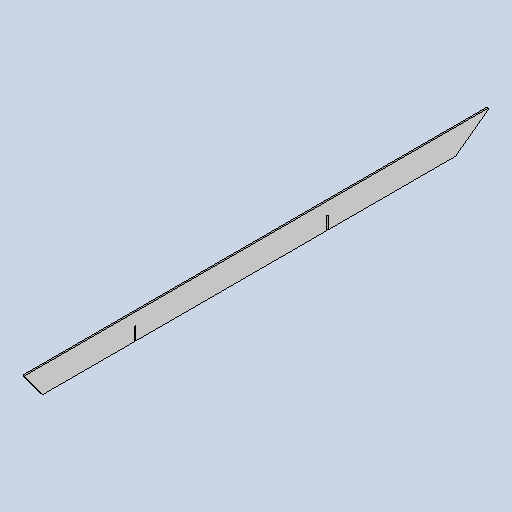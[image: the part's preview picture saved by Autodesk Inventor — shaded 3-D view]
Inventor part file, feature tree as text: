
AUTODESK INVENTOR PART (.ipt)
format: ipt  version: 2025 (Build 290162010, 162A)  size: 151,040 bytes
history: native  units: mm
features: other x3, sketch x2, sheet_metal_op x1, chamfer x1, extrude x1
ambient origin geometry x8: Origin, YZ Plane, XZ Plane, XY Plane, X Axis, Y Axis, Z Axis, Center Point
bodies: Body1 (feature_tree)
feature tree (8):
  sheet_metal_op  "Face1"
  other  "Corner Chamfer1"
  chamfer  "Corner Round1"
  extrude  "Extrusion1"  Depth=920.0mm
  sketch  "Sketch2"  dims[d3=380.0mm d6=380.0mm d7=380.0mm d28=920.0mm]
  other  "Plate2"
  sketch  "Sketch3"  dims[d29=50.0mm d30=3.0mm d31=6.335545mm d32=9.372418mm d33=3.0mm d34=6.0mm d35=45.0deg d36=9.372418mm d37=6.0mm d38=219.04mm d39=26.0mm d40=3.0mm d41=219.04mm d42=599.04mm d43=3.0mm d44=26.0mm d45=0.0mm d46=0.0mm]
  other  "Definition1"
